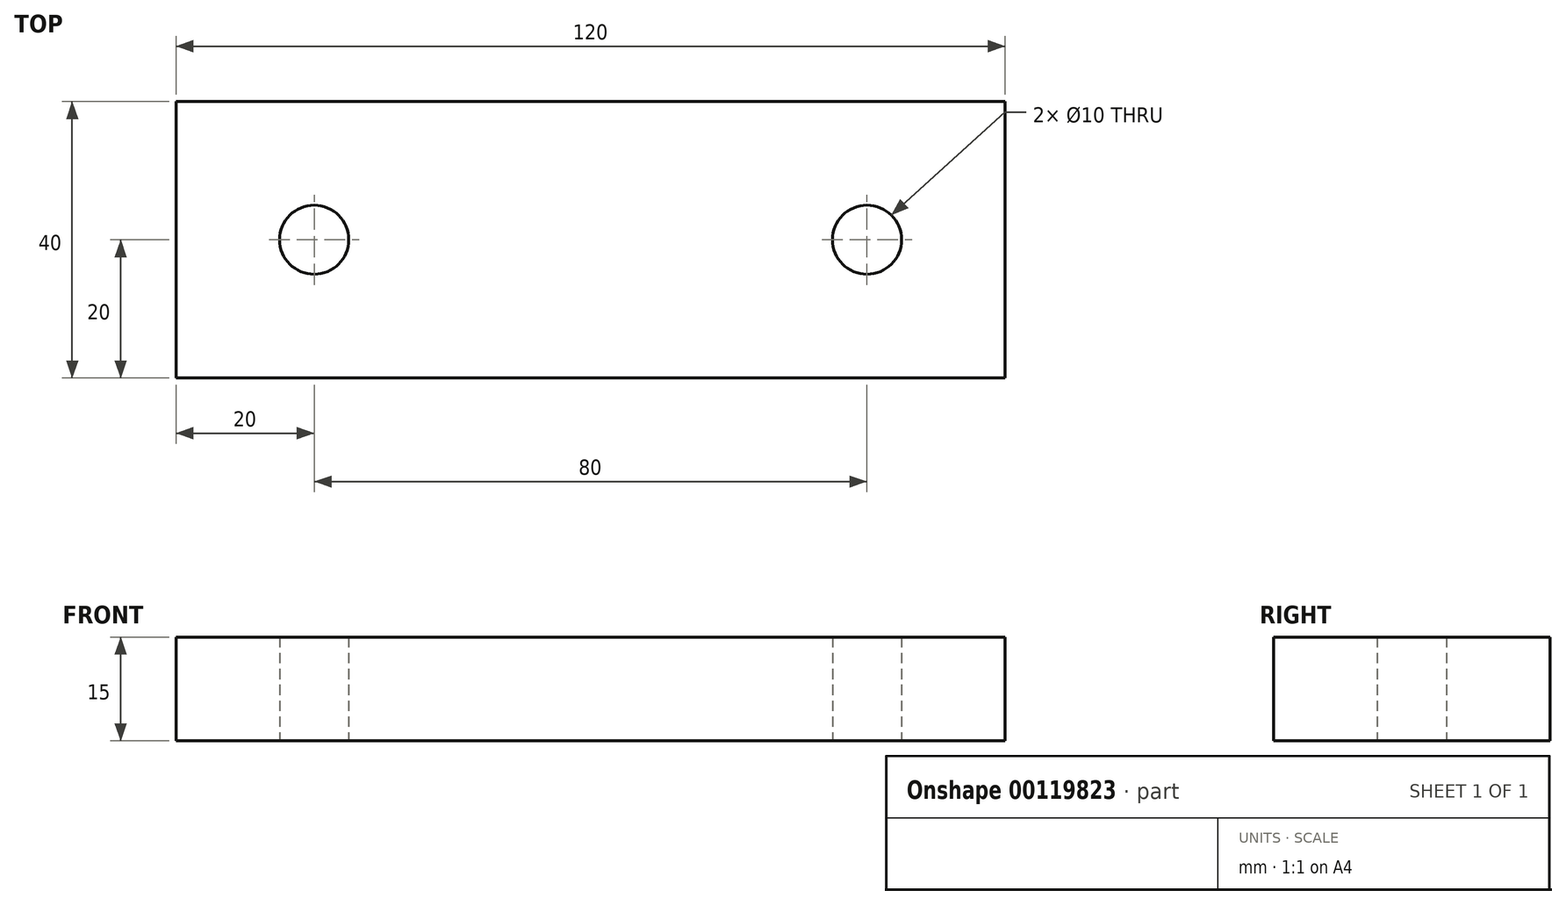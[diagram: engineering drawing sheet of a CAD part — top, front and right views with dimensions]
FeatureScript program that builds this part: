
annotation { "Feature Type Name" : "Feature", "Feature Type Description" : "" }
export const myFeature = defineFeature(function(context is Context, id is Id, definition is map)
    precondition{}
    {
        {
            var Q0;
            Q0=qCreatedBy(makeId("Top.planeOp"),FACE);
            var sketch = newSketch(context, id + "F0", { "sketchPlane" : qUnion([Q0])});
            skLineSegment(sketch, "E0.bottom", {"start": v(-60, 20) * mm, "end": v(60, 20) * mm});
            skLineSegment(sketch, "E0.top", {"start": v(-60, -20) * mm, "end": v(60, -20) * mm});
            skLineSegment(sketch, "E0.left", {"start": v(-60, 20) * mm, "end": v(-60, -20) * mm});
            skLineSegment(sketch, "E0.right", {"start": v(60, 20) * mm, "end": v(60, -20) * mm});
            skCircle(sketch, "E1", {"center": v(-40, 0) * mm, "radius": 5 * mm});
            skCircle(sketch, "E2", {"center": v(40, 0) * mm, "radius": 5 * mm});
            skSolve(sketch);
        }
        {
            var Q0;
            Q0=qSketchRegion(id+"F0",true);
            extrude(context, id + "F1", {"entities" : qUnion([Q0]), "depth" : 15 * mm});
        }
    });
